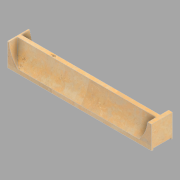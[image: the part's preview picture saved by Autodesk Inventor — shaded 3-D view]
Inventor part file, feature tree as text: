
AUTODESK INVENTOR PART (.ipt)
format: ipt  version: 2022.2 (Build 262287010, 287A)  size: 174,080 bytes
history: native  units: in
note: dims shown in document units (in); Inventor stores cm internally (conversion verified against a paired STEP export)
features: other x1, plane x1, extrude x1, sketch x1
ambient origin geometry x8: Origin, YZ Plane, XZ Plane, XY Plane, X Axis, Y Axis, Z Axis, Center Point
bodies: Solid1 (feature_tree)
feature tree (4):
  other  "North (6) (1)"
  plane  "Work Plane1"
  extrude  "Extrusion1"  Depth=1.0in
  sketch  "Sketch1"  dims[d2=-18.3125in d3=1.0in d4=1.0in d5=8.75in d6=8.75in d7=0.375in d8=0.375in d9=0.375in d10=1.0in d11=5.75in d12=18.1875in d13=16.9375in d14=0.0in d15=0.0in]
